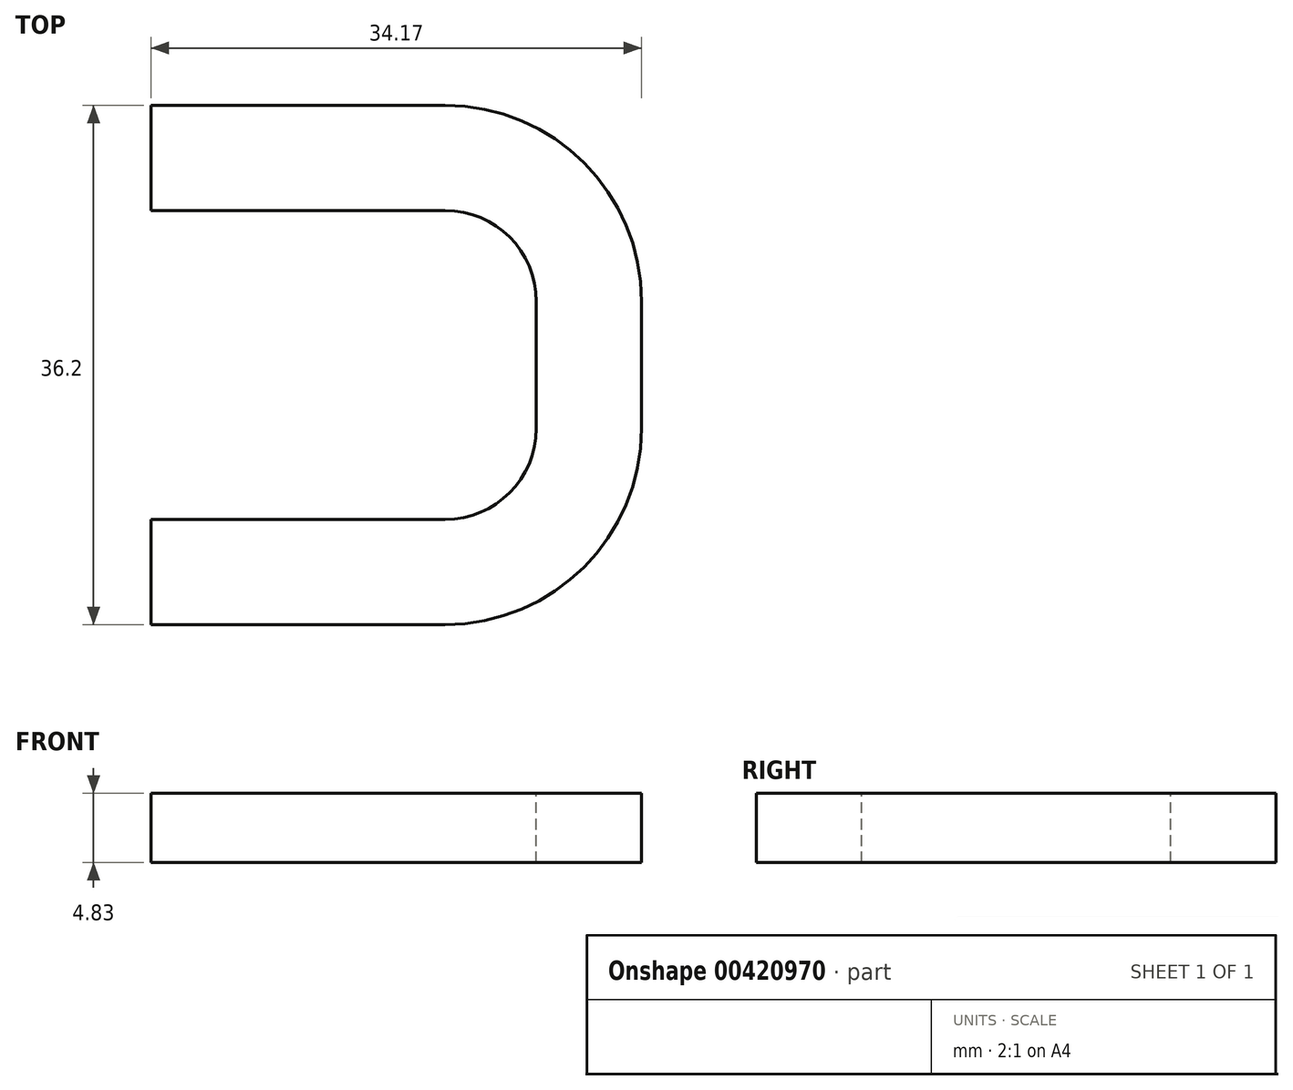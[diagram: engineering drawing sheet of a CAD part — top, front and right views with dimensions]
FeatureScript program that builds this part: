
annotation { "Feature Type Name" : "Feature", "Feature Type Description" : "" }
export const myFeature = defineFeature(function(context is Context, id is Id, definition is map)
    precondition{}
    {
        {
            var Q0;
            Q0=qCreatedBy(makeId("Top.planeOp"),FACE);
            var sketch = newSketch(context, id + "F0", { "sketchPlane" : qUnion([Q0])});
            skLineSegment(sketch, "E0", {"start": v(0, 0) * mm, "end": v(20.5, 0) * mm});
            skLineSegment(sketch, "E1", {"start": v(26.84, -6.35) * mm, "end": v(26.84, -15.2) * mm});
            skLineSegment(sketch, "E2", {"start": v(20.5, -21.54) * mm, "end": v(0, -21.54) * mm});
            skPoint(sketch, "E3.visualSharp", {"position": v(26.84, -21.54) * mm});
            skArc(sketch, "E3.filletArc", {"start": v(20.5, -21.54) * mm, "mid": v(24.98, -19.68) * mm, "end": v(26.84, -15.2) * mm});
            skPoint(sketch, "E4.visualSharp", {"position": v(26.84, 0) * mm});
            skArc(sketch, "E4.filletArc", {"start": v(26.84, -6.35) * mm, "mid": v(24.98, -1.86) * mm, "end": v(20.5, 0) * mm});
            skSolve(sketch);
        }
        {
            var Q0;
            Q0=qCreatedBy(makeId("Right.planeOp"),FACE);
            var sketch = newSketch(context, id + "F1", { "sketchPlane" : qUnion([Q0])});
            skLineSegment(sketch, "E5.bottom", {"start": v(0, 0) * mm, "end": v(7.33, 0) * mm});
            skLineSegment(sketch, "E5.top", {"start": v(0, 4.83) * mm, "end": v(7.33, 4.83) * mm});
            skLineSegment(sketch, "E5.left", {"start": v(0, 0) * mm, "end": v(0, 4.83) * mm});
            skLineSegment(sketch, "E5.right", {"start": v(7.33, 0) * mm, "end": v(7.33, 4.83) * mm});
            skSolve(sketch);
        }
        {
            var Q0;
            Q0=makeQuery(id+"F1.imprint","IMPRINT",FACE,{"disambiguationData":[TD([[makeQuery(id+"F1.imprint","IMPRINT",EDGE,{"derivedFrom":sQuery(id+"F1.wireOp",EDGE,"E5.bottom")}),1.0]])]});
            var Q1;
            Q1=sQuery(id+"F0.wireOp",EDGE,"E0");
            var Q2;
            Q2=sQuery(id+"F0.wireOp",EDGE,"E4.filletArc");
            var Q3;
            Q3=sQuery(id+"F0.wireOp",EDGE,"E1");
            var Q4;
            Q4=sQuery(id+"F0.wireOp",EDGE,"E3.filletArc");
            var Q5;
            Q5=sQuery(id+"F0.wireOp",EDGE,"E2");
            sweep(context, id + "F2", {"profiles" : qUnion([Q0]), "path" : qUnion([Q1, Q2, Q3, Q4, Q5])});
        }
    });
